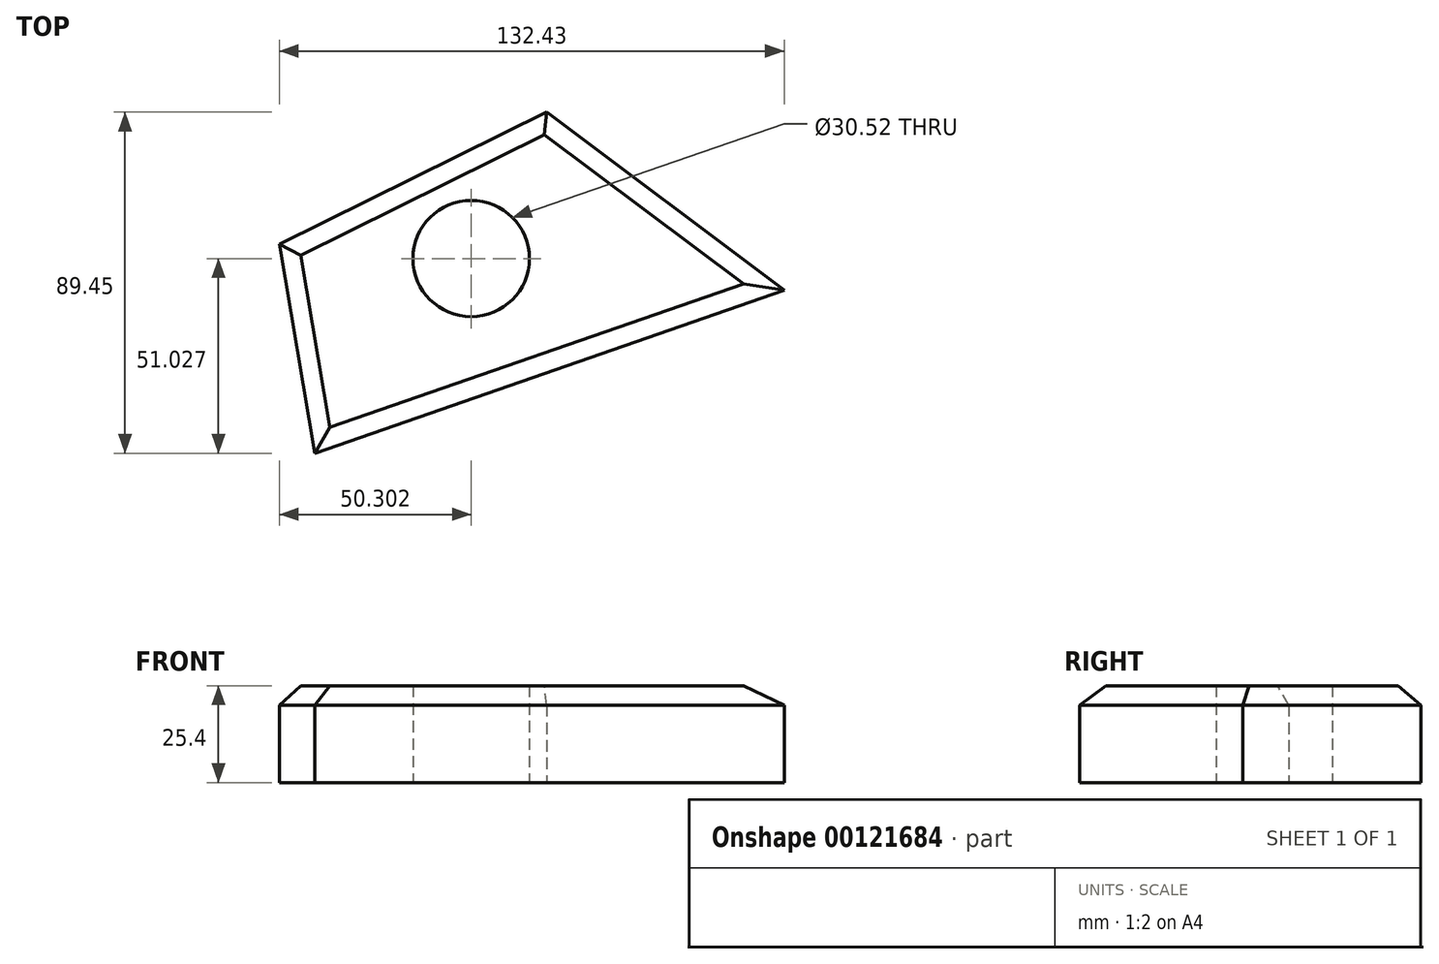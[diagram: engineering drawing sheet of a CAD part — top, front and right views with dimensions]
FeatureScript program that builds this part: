
annotation { "Feature Type Name" : "Feature", "Feature Type Description" : "" }
export const myFeature = defineFeature(function(context is Context, id is Id, definition is map)
    precondition{}
    {
        {
            var Q0;
            Q0=qCreatedBy(makeId("Top.planeOp"),FACE);
            var sketch = newSketch(context, id + "F0", { "sketchPlane" : qUnion([Q0])});
            skLineSegment(sketch, "E0", {"start": v(-128.28, 0) * mm, "end": v(-119.03, -54.75) * mm});
            skLineSegment(sketch, "E1", {"start": v(-119.03, -54.75) * mm, "end": v(4.15, -12) * mm});
            skLineSegment(sketch, "E2", {"start": v(4.15, -12) * mm, "end": v(-58.2, 34.7) * mm});
            skLineSegment(sketch, "E3", {"start": v(-58.2, 34.7) * mm, "end": v(-128.28, 0) * mm});
            skCircle(sketch, "E4", {"center": v(-77.98, -3.72) * mm, "radius": 15.26 * mm});
            skSolve(sketch);
        }
        {
            var Q0;
            Q0=makeQuery(id+"F0.imprint","IMPRINT",FACE,{"disambiguationData":[TD([[makeQuery(id+"F0.imprint","IMPRINT",EDGE,{"derivedFrom":sQuery(id+"F0.wireOp",EDGE,"E0")}),1.0]])]});
            extrude(context, id + "F1", {"entities" : qUnion([Q0]), "depth" : 25.4 * mm});
        }
        {
            var Q0;
            Q0=makeQuery(id+"F1.opExtrude","CAP_EDGE",EDGE,{"disambiguationData":[OSD([sQuery(id+"F0.wireOp",EDGE,"E3")])],"isStart":false});
            var Q1;
            Q1=makeQuery(id+"F1.opExtrude","CAP_EDGE",EDGE,{"disambiguationData":[OSD([sQuery(id+"F0.wireOp",EDGE,"E0")])],"isStart":false});
            var Q2;
            Q2=makeQuery(id+"F1.opExtrude","CAP_EDGE",EDGE,{"disambiguationData":[OSD([sQuery(id+"F0.wireOp",EDGE,"E1")])],"isStart":false});
            var Q3;
            Q3=makeQuery(id+"F1.opExtrude","CAP_EDGE",EDGE,{"disambiguationData":[OSD([sQuery(id+"F0.wireOp",EDGE,"E2")])],"isStart":false});
            chamfer(context, id + "F2", {"entities" : qUnion([Q0, Q1, Q2, Q3]), "width" : 5.08 * mm, "tangentPropagation" : true});
        }
    });
